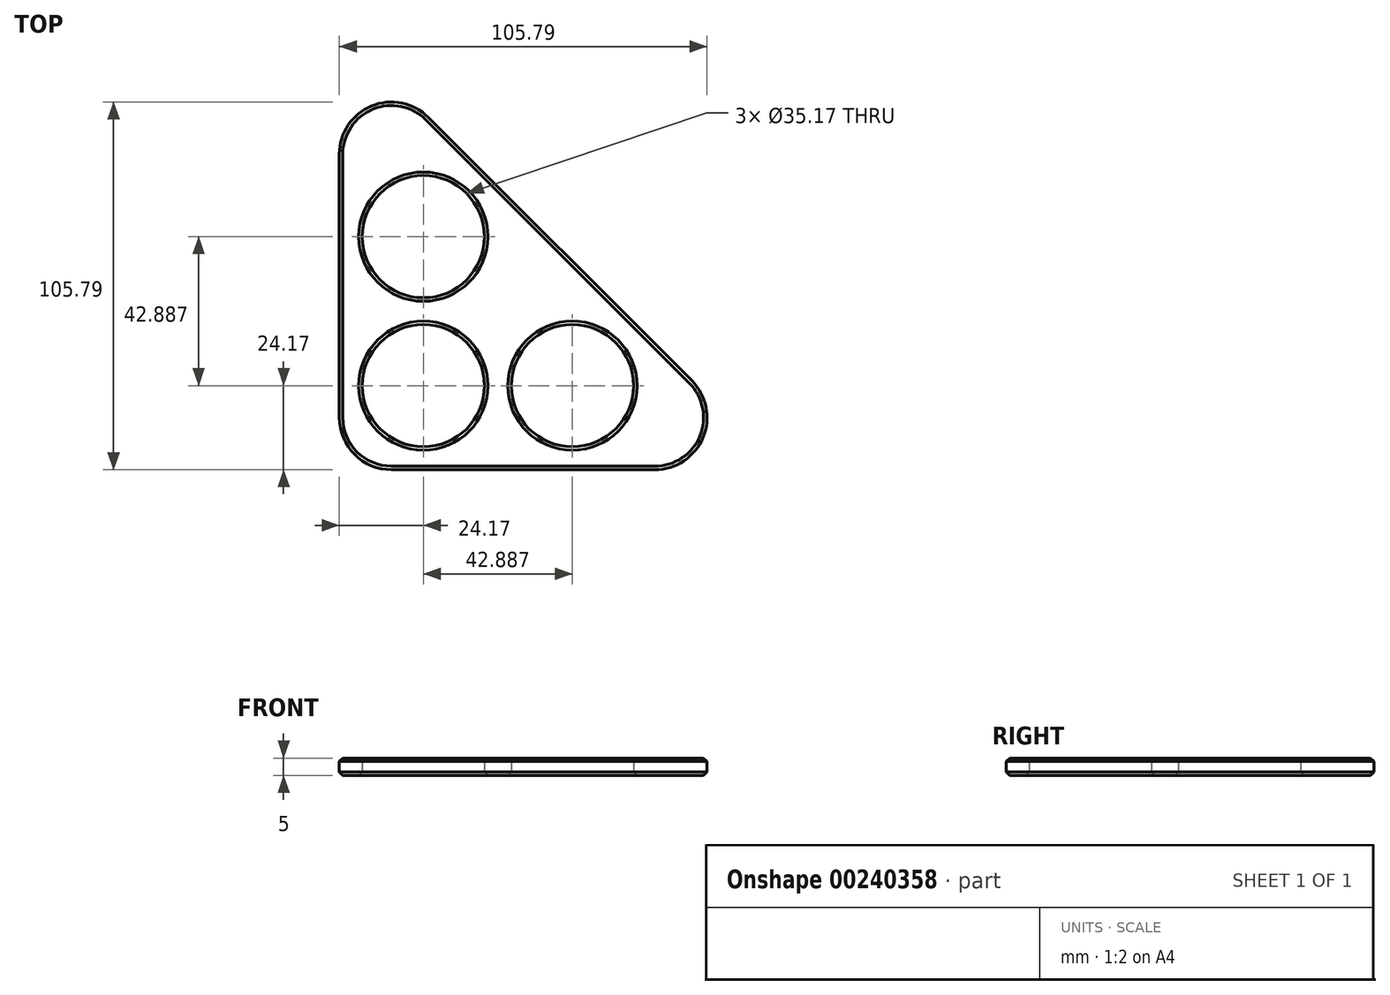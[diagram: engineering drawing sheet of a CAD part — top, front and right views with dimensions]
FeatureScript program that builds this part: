
annotation { "Feature Type Name" : "Feature", "Feature Type Description" : "" }
export const myFeature = defineFeature(function(context is Context, id is Id, definition is map)
    precondition{}
    {
        {
            var Q0;
            Q0=qCreatedBy(makeId("Top.planeOp"),FACE);
            var sketch = newSketch(context, id + "F0", { "sketchPlane" : qUnion([Q0])});
            skLineSegment(sketch, "E0", {"start": v(0, 0) * mm, "end": v(127, 0) * mm});
            skLineSegment(sketch, "E1", {"start": v(127, 0) * mm, "end": v(0, 127) * mm});
            skLineSegment(sketch, "E2", {"start": v(0, 127) * mm, "end": v(0, 0) * mm});
            skCircle(sketch, "E3", {"center": v(24.17, 67.06) * mm, "radius": 17.58 * mm});
            skCircle(sketch, "E4", {"center": v(24.17, 24.17) * mm, "radius": 17.58 * mm});
            skCircle(sketch, "E5", {"center": v(67.06, 24.17) * mm, "radius": 17.58 * mm});
            skLineSegment(sketch, "E6", {"start": v(0, 0) * mm, "end": v(63.5, 63.5) * mm, "construction": true});
            skSolve(sketch);
        }
        {
            var Q0;
            Q0 = qSketchRegion(id + "F0", true);
            extrude(context, id + "F1", {"entities" : qUnion([Q0]), "depth" : 5 * mm});
        }
        {
            var Q0;
            Q0=makeQuery(id+"F1.opExtrude","SWEPT_EDGE",EDGE,{"disambiguationData":[OSD([sQuery(id+"F0.wireOp",EDGE,"E0"),sQuery(id+"F0.wireOp",EDGE,"E1")])]});
            var Q1;
            Q1=makeQuery(id+"F1.opExtrude","SWEPT_EDGE",EDGE,{"disambiguationData":[OSD([sQuery(id+"F0.wireOp",EDGE,"E0"),sQuery(id+"F0.wireOp",EDGE,"E2")])]});
            var Q2;
            Q2=makeQuery(id+"F1.opExtrude","SWEPT_EDGE",EDGE,{"disambiguationData":[OSD([sQuery(id+"F0.wireOp",EDGE,"E2"),sQuery(id+"F0.wireOp",EDGE,"1ZePDVp7-iO4U-aMN7-2dtA-EEiYL6tTJ1W2")])]});
            var Q3;
            Q3=makeQuery(id+"F1.opExtrude","SWEPT_EDGE",EDGE,{"disambiguationData":[OSD([sQuery(id+"F0.wireOp",EDGE,"E1"),sQuery(id+"F0.wireOp",EDGE,"1ZePDVp7-iO4U-aMN7-2dtA-EEiYL6tTJ1W2")])]});
            fillet(context, id + "F2", {"entities" : qUnion([Q0, Q1, Q2, Q3]), "radius" : 15 * mm, "tangentPropagation" : true, "allowEdgeOverflow" : false});
        }
        {
            var Q0;
            {var subQ0=sQuery(id+"F0.wireOp",EDGE,"E1");var subQ1=sQuery(id+"F0.wireOp",EDGE,"E0");Q0=makeQuery(id+"F2.opFillet","BLEND_EDGE",EDGE,{"blendedFrom":[makeQuery(id+"F1.opExtrude","SWEPT_EDGE",EDGE,{"disambiguationData":[OSD([subQ1,subQ0])]}),makeQuery(id+"F1.opExtrude","CAP_FACE",FACE,{"disambiguationData":[OSD([subQ1,subQ0,sQuery(id+"F0.wireOp",EDGE,"E2"),sQuery(id+"F0.wireOp",EDGE,"7FbShTeD-oCoi-vzZg-R016-UevPAgJqWab2"),sQuery(id+"F0.wireOp",EDGE,"RwQlDSzC-lgRK-1khT-X5PZ-zoZjuITexlYm"),sQuery(id+"F0.wireOp",EDGE,"8e7d9a8c-3046-4ff8-93a0-6e85653d0236.trimOffspring")])],"isStart":false})],"blendedInto":[makeQuery(id+"F1.opExtrude","CAP_FACE",FACE,{"disambiguationData":[OSD([subQ1,subQ0,sQuery(id+"F0.wireOp",EDGE,"E2"),sQuery(id+"F0.wireOp",EDGE,"7FbShTeD-oCoi-vzZg-R016-UevPAgJqWab2"),sQuery(id+"F0.wireOp",EDGE,"RwQlDSzC-lgRK-1khT-X5PZ-zoZjuITexlYm"),sQuery(id+"F0.wireOp",EDGE,"8e7d9a8c-3046-4ff8-93a0-6e85653d0236.trimOffspring")])],"isStart":false})]});}
            var Q1;
            Q1=makeQuery(id+"F1.opExtrude","CAP_EDGE",EDGE,{"disambiguationData":[OSD([sQuery(id+"F0.wireOp",EDGE,"E1")])],"isStart":true});
            var Q2;
            Q2=makeQuery(id+"F1.opExtrude","CAP_EDGE",EDGE,{"disambiguationData":[OSD([sQuery(id+"F0.wireOp",EDGE,"7FbShTeD-oCoi-vzZg-R016-UevPAgJqWab2")])],"isStart":false});
            var Q3;
            Q3=makeQuery(id+"F1.opExtrude","CAP_EDGE",EDGE,{"disambiguationData":[OSD([sQuery(id+"F0.wireOp",EDGE,"E4")])],"isStart":false});
            var Q4;
            Q4=makeQuery(id+"F1.opExtrude","CAP_EDGE",EDGE,{"disambiguationData":[OSD([sQuery(id+"F0.wireOp",EDGE,"E5")])],"isStart":false});
            var Q5;
            Q5=makeQuery(id+"F1.opExtrude","CAP_EDGE",EDGE,{"disambiguationData":[OSD([sQuery(id+"F0.wireOp",EDGE,"E3")])],"isStart":true});
            var Q6;
            Q6=makeQuery(id+"F1.opExtrude","CAP_EDGE",EDGE,{"disambiguationData":[OSD([sQuery(id+"F0.wireOp",EDGE,"E4")])],"isStart":true});
            var Q7;
            Q7=makeQuery(id+"F1.opExtrude","CAP_EDGE",EDGE,{"disambiguationData":[OSD([sQuery(id+"F0.wireOp",EDGE,"E5")])],"isStart":true});
            var Q8;
            Q8=makeQuery(id+"F1.opExtrude","CAP_EDGE",EDGE,{"disambiguationData":[OSD([sQuery(id+"F0.wireOp",EDGE,"E3")])],"isStart":false});
            chamfer(context, id + "F3", {"entities" : qUnion([Q0, Q1, Q2, Q3, Q4, Q5, Q6, Q7, Q8]), "width" : 1 * mm, "tangentPropagation" : true});
        }
    });
